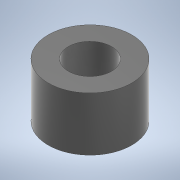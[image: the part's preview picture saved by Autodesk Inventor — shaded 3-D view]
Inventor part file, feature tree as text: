
AUTODESK INVENTOR PART (.ipt)
format: ipt  version: 2020 (Build 240168000, 168)  size: 219,648 bytes
history: native  units: mm
features: extrude x1, sketch x1
ambient origin geometry x8: Origin, YZ Plane, XZ Plane, XY Plane, X Axis, Y Axis, Z Axis, Center Point
bodies: Volumenkörper1 (feature_tree)
feature tree (2):
  extrude  "Extrusion1"  Depth=4.0mm
  sketch  "Skizze1"  dims[d0=3.2mm d1=1.5mm d2=4.0mm d3=0.0mm]
